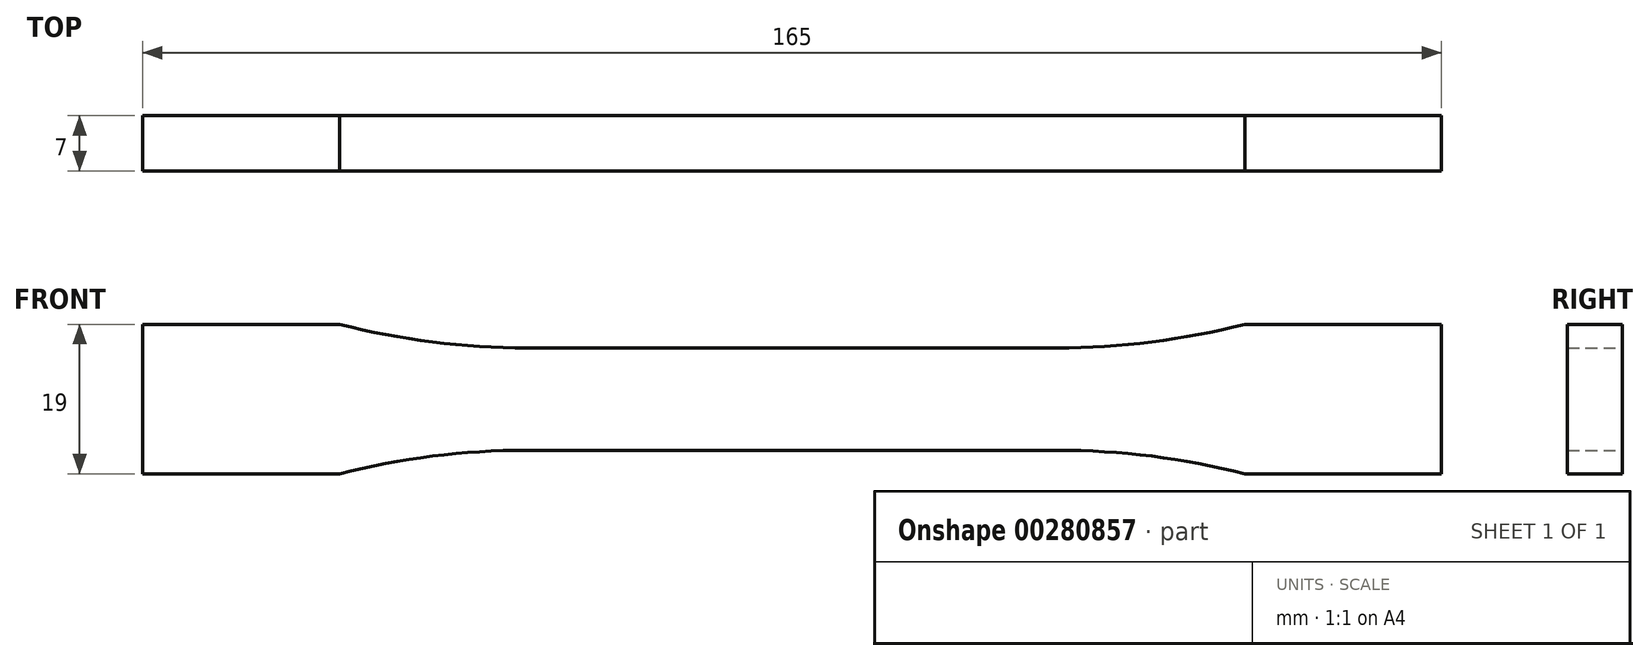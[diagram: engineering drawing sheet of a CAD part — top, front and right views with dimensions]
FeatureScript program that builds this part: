
annotation { "Feature Type Name" : "Feature", "Feature Type Description" : "" }
export const myFeature = defineFeature(function(context is Context, id is Id, definition is map)
    precondition{}
    {
        {
            var Q0;
            Q0=qCreatedBy(makeId("Front.planeOp"),FACE);
            var sketch = newSketch(context, id + "F0", { "sketchPlane" : qUnion([Q0])});
            skLineSegment(sketch, "E0", {"start": v(0, 6.5) * mm, "end": v(33.69, 6.5) * mm});
            skArc(sketch, "E1", {"start": v(33.69, 6.5) * mm, "mid": v(45.69, 7.25) * mm, "end": v(57.5, 9.5) * mm});
            skLineSegment(sketch, "E2", {"start": v(57.5, 9.5) * mm, "end": v(82.5, 9.5) * mm});
            skLineSegment(sketch, "E3.MirrorCS", {"start": v(0, -6.5) * mm, "end": v(33.69, -6.5) * mm});
            skArc(sketch, "E4.MirrorCS", {"start": v(33.69, -6.5) * mm, "mid": v(45.69, -7.25) * mm, "end": v(57.5, -9.5) * mm});
            skLineSegment(sketch, "E5.MirrorCS", {"start": v(57.5, -9.5) * mm, "end": v(82.5, -9.5) * mm});
            skLineSegment(sketch, "E6.MirrorCS", {"start": v(0, 6.5) * mm, "end": v(-33.69, 6.5) * mm});
            skArc(sketch, "E7.MirrorCS", {"start": v(-33.69, 6.5) * mm, "mid": v(-45.69, 7.25) * mm, "end": v(-57.5, 9.5) * mm});
            skArc(sketch, "E8.MirrorCS", {"start": v(-33.69, -6.5) * mm, "mid": v(-45.69, -7.25) * mm, "end": v(-57.5, -9.5) * mm});
            skLineSegment(sketch, "E9.MirrorCS", {"start": v(-57.5, 9.5) * mm, "end": v(-82.5, 9.5) * mm});
            skLineSegment(sketch, "E10.MirrorCS", {"start": v(-57.5, -9.5) * mm, "end": v(-82.5, -9.5) * mm});
            skLineSegment(sketch, "E11.MirrorCS", {"start": v(0, -6.5) * mm, "end": v(-33.69, -6.5) * mm});
            skLineSegment(sketch, "E12", {"start": v(-82.5, 9.5) * mm, "end": v(-82.5, -9.5) * mm});
            skLineSegment(sketch, "E13", {"start": v(82.5, 9.5) * mm, "end": v(82.5, -9.5) * mm});
            skSolve(sketch);
        }
        {
            var Q0;
            Q0 = qSketchRegion(id + "F0", true);
            extrude(context, id + "F1", {"entities" : qUnion([Q0]), "endBound" : BoundingType.SYMMETRIC, "depth" : 7 * mm});
        }
    });
